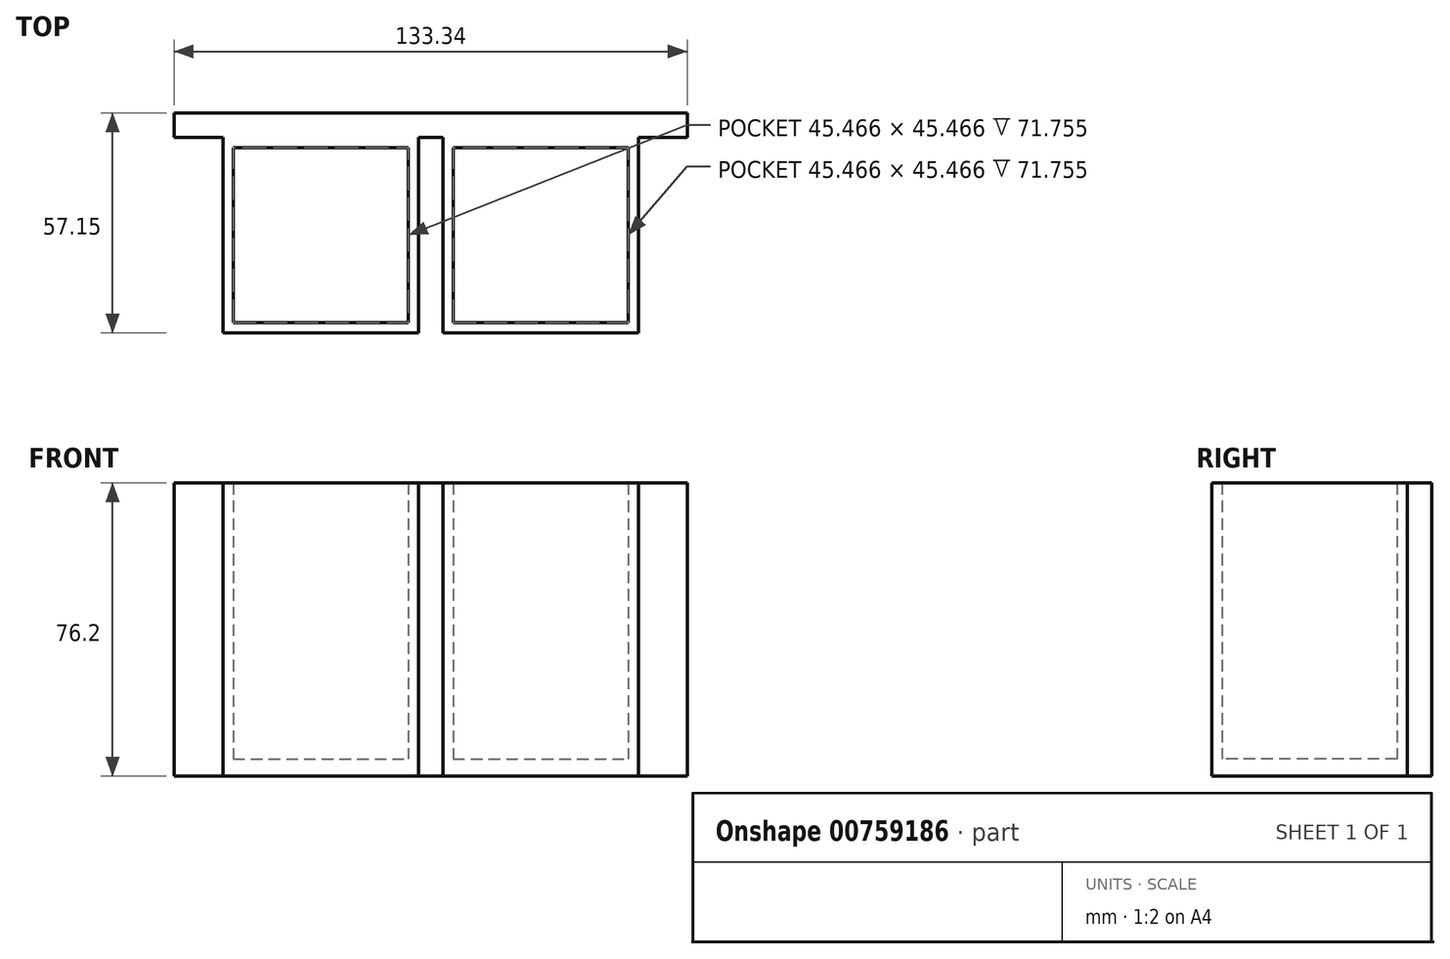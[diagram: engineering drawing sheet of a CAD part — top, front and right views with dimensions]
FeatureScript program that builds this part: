
annotation { "Feature Type Name" : "Feature", "Feature Type Description" : "" }
export const myFeature = defineFeature(function(context is Context, id is Id, definition is map)
    precondition{}
    {
        {
            var Q0;
            Q0=qCreatedBy(makeId("Front.planeOp"),FACE);
            var sketch = newSketch(context, id + "F0", { "sketchPlane" : qUnion([Q0])});
            skLineSegment(sketch, "E0.bottom", {"start": v(66.67, 38.1) * mm, "end": v(-66.68, 38.1) * mm});
            skLineSegment(sketch, "E0.top", {"start": v(66.68, -38.1) * mm, "end": v(-66.67, -38.1) * mm});
            skLineSegment(sketch, "E0.left", {"start": v(66.67, 38.1) * mm, "end": v(66.68, -38.1) * mm});
            skLineSegment(sketch, "E0.right", {"start": v(-66.68, 38.1) * mm, "end": v(-66.67, -38.1) * mm});
            skPoint(sketch, "E0.middle", {"position": v(0, 0) * mm});
            skSolve(sketch);
        }
        {
            var Q0;
            Q0=qCreatedBy(makeId("Top.planeOp"),FACE);
            var sketch = newSketch(context, id + "F1", { "sketchPlane" : qUnion([Q0])});
            skLineSegment(sketch, "E1.bottom", {"start": v(-53.98, 0) * mm, "end": v(53.98, 0) * mm});
            skLineSegment(sketch, "E1.top", {"start": v(-53.98, -50.8) * mm, "end": v(53.98, -50.8) * mm});
            skLineSegment(sketch, "E1.left", {"start": v(-53.98, 0) * mm, "end": v(-53.98, -50.8) * mm});
            skLineSegment(sketch, "E1.right", {"start": v(53.98, 0) * mm, "end": v(53.98, -50.8) * mm});
            skLineSegment(sketch, "E2.bottom", {"start": v(-51.3, -2.67) * mm, "end": v(-5.84, -2.67) * mm});
            skLineSegment(sketch, "E2.top", {"start": v(-51.3, -48.13) * mm, "end": v(-5.84, -48.13) * mm});
            skLineSegment(sketch, "E2.left", {"start": v(-51.3, -2.67) * mm, "end": v(-51.3, -48.13) * mm});
            skLineSegment(sketch, "E2.right", {"start": v(-5.84, -2.67) * mm, "end": v(-5.84, -48.13) * mm});
            skLineSegment(sketch, "E3.bottom", {"start": v(5.84, -2.67) * mm, "end": v(51.3, -2.67) * mm});
            skLineSegment(sketch, "E3.top", {"start": v(5.84, -48.13) * mm, "end": v(51.3, -48.13) * mm});
            skLineSegment(sketch, "E3.left", {"start": v(5.84, -2.67) * mm, "end": v(5.84, -48.13) * mm});
            skLineSegment(sketch, "E3.right", {"start": v(51.3, -2.67) * mm, "end": v(51.3, -48.13) * mm});
            skLineSegment(sketch, "E4", {"start": v(-3.18, 0) * mm, "end": v(-3.18, -50.8) * mm});
            skLineSegment(sketch, "E5", {"start": v(3.17, 0) * mm, "end": v(3.17, -50.8) * mm});
            skPoint(sketch, "E6", {"position": v(28.58, 0) * mm});
            skSolve(sketch);
        }
        {
            var Q0;
            Q0=makeQuery(id+"F0.imprint","IMPRINT",FACE,{"disambiguationData":[TD([[makeQuery(id+"F0.imprint","IMPRINT",EDGE,{"derivedFrom":sQuery(id+"F0.wireOp",EDGE,"E0.bottom")}),1.0]])]});
            extrude(context, id + "F2", {"entities" : qUnion([Q0]), "oppositeDirection" : true, "depth" : 6.35 * mm, "offsetDistance" : 25.4 * mm});
        }
        {
            var Q0;
            {var subQ0=sQuery(id+"F1.wireOp",EDGE,"E1.left");Q0=makeQuery(id+"F1.imprint","IMPRINT",FACE,{"disambiguationData":[TD([[makeQuery(id+"F1.imprint","IMPRINT",EDGE,{"derivedFrom":subQ0}),1.0]])]});}
            var Q1;
            {var subQ0=sQuery(id+"F1.wireOp",EDGE,"E1.right");Q1=makeQuery(id+"F1.imprint","IMPRINT",FACE,{"disambiguationData":[TD([[makeQuery(id+"F1.imprint","IMPRINT",EDGE,{"derivedFrom":subQ0}),-1.0]])]});}
            extrude(context, id + "F3", {"entities" : qUnion([Q0, Q1]), "operationType" : NewBodyOperationType.ADD, "endBound" : BoundingType.SYMMETRIC, "depth" : 76.2 * mm, "offsetDistance" : 25.4 * mm});
        }
        {
            var Q0;
            Q0=makeQuery(id+"F1.imprint","IMPRINT",FACE,{"disambiguationData":[TD([[makeQuery(id+"F1.imprint","IMPRINT",EDGE,{"derivedFrom":sQuery(id+"F1.wireOp",EDGE,"E2.bottom")}),-1.0]])]});
            var Q1;
            Q1=makeQuery(id+"F1.imprint","IMPRINT",FACE,{"disambiguationData":[TD([[makeQuery(id+"F1.imprint","IMPRINT",EDGE,{"derivedFrom":sQuery(id+"F1.wireOp",EDGE,"E3.bottom")}),-1.0]])]});
            extrude(context, id + "F4", {"entities" : qUnion([Q0, Q1]), "operationType" : NewBodyOperationType.ADD, "oppositeDirection" : true, "depth" : 38.1 * mm, "offsetDistance" : 25.4 * mm, "hasSecondDirection" : true, "secondDirectionOppositeDirection" : true, "secondDirectionDepth" : 33.65 * mm});
        }
    });
